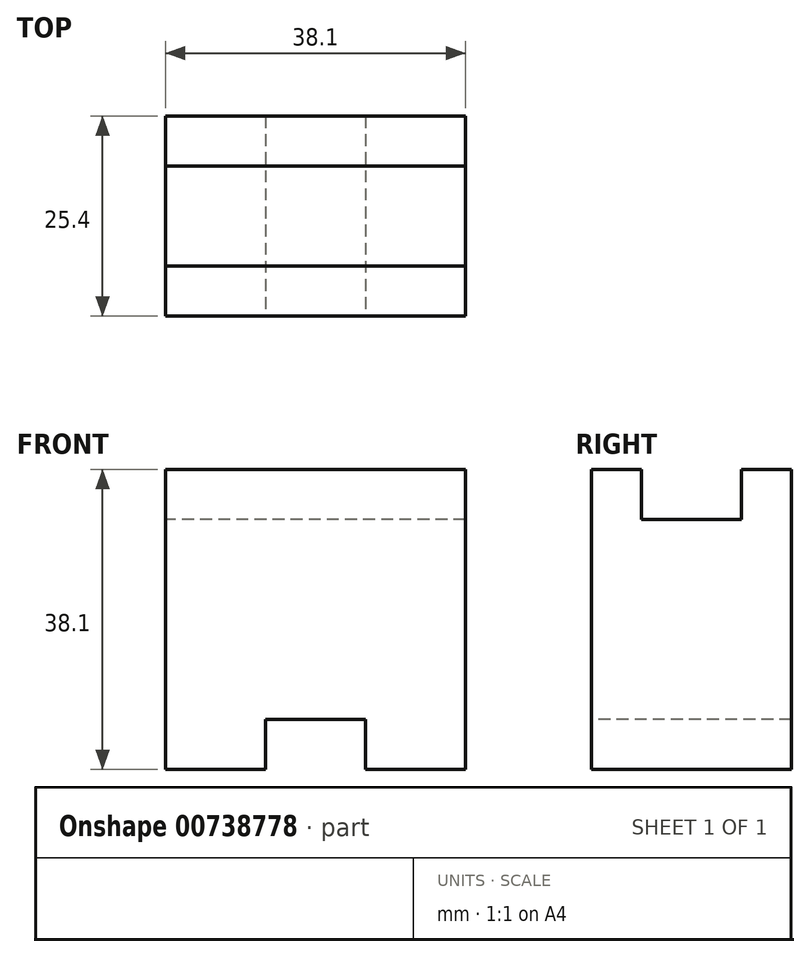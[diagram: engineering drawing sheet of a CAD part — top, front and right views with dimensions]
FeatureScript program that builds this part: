
annotation { "Feature Type Name" : "Feature", "Feature Type Description" : "" }
export const myFeature = defineFeature(function(context is Context, id is Id, definition is map)
    precondition{}
    {
        {
            var Q0;
            Q0=qCreatedBy(makeId("Right.planeOp"),FACE);
            var sketch = newSketch(context, id + "F0", { "sketchPlane" : qUnion([Q0])});
            skLineSegment(sketch, "E0", {"start": v(0, 0) * mm, "end": v(0, 38.1) * mm});
            skLineSegment(sketch, "E1", {"start": v(0, 38.1) * mm, "end": v(6.35, 38.1) * mm});
            skLineSegment(sketch, "E2", {"start": v(6.35, 38.1) * mm, "end": v(6.35, 31.75) * mm});
            skLineSegment(sketch, "E3", {"start": v(6.35, 31.75) * mm, "end": v(19.05, 31.75) * mm});
            skLineSegment(sketch, "E4", {"start": v(19.05, 31.75) * mm, "end": v(19.05, 38.1) * mm});
            skLineSegment(sketch, "E5", {"start": v(19.05, 38.1) * mm, "end": v(25.4, 38.1) * mm});
            skLineSegment(sketch, "E6", {"start": v(25.4, 38.1) * mm, "end": v(25.4, 0) * mm});
            skLineSegment(sketch, "E7", {"start": v(25.4, 0) * mm, "end": v(0, 0) * mm});
            skSolve(sketch);
        }
        {
            var Q0;
            Q0 = qSketchRegion(id + "F0", true);
            extrude(context, id + "F1", {"entities" : qUnion([Q0]), "depth" : 38.1 * mm, "offsetDistance" : 25.4 * mm});
        }
        {
            var Q0;
            Q0=qCreatedBy(makeId("Front.planeOp"),FACE);
            var sketch = newSketch(context, id + "F2", { "sketchPlane" : qUnion([Q0])});
            skLineSegment(sketch, "E8", {"start": v(25.4, 0) * mm, "end": v(25.4, 6.35) * mm});
            skLineSegment(sketch, "E9", {"start": v(25.4, 6.35) * mm, "end": v(12.7, 6.35) * mm});
            skLineSegment(sketch, "E10", {"start": v(12.7, 6.35) * mm, "end": v(12.7, 0) * mm});
            skLineSegment(sketch, "E11", {"start": v(12.7, 0) * mm, "end": v(25.4, 0) * mm});
            skSolve(sketch);
        }
        {
            var Q0;
            Q0 = qSketchRegion(id + "F2", true);
            extrude(context, id + "F3", {"entities" : qUnion([Q0]), "operationType" : NewBodyOperationType.REMOVE, "oppositeDirection" : true, "depth" : 25.4 * mm, "offsetDistance" : 25.4 * mm});
        }
    });
